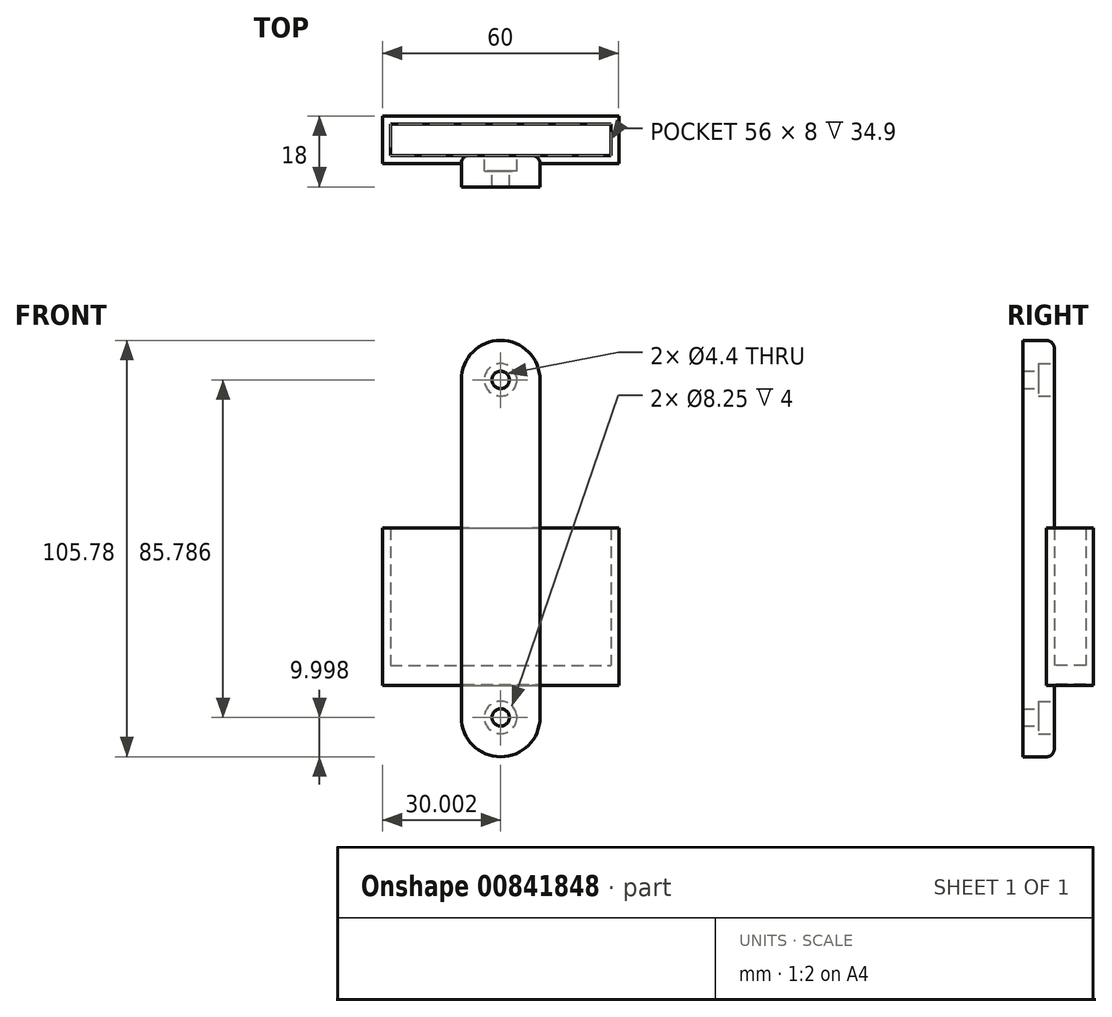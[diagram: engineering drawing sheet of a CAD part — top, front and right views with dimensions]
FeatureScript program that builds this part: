
annotation { "Feature Type Name" : "Feature", "Feature Type Description" : "" }
export const myFeature = defineFeature(function(context is Context, id is Id, definition is map)
    precondition{}
    {
        {
            var Q0;
            Q0=qCreatedBy(makeId("Top.planeOp"),FACE);
            var sketch = newSketch(context, id + "F0", { "sketchPlane" : qUnion([Q0])});
            skLineSegment(sketch, "E0.bottom", {"start": v(-46.7, 10) * mm, "end": v(-26.7, 10) * mm});
            skLineSegment(sketch, "E0.top", {"start": v(-46.7, -2) * mm, "end": v(13.3, -2) * mm});
            skLineSegment(sketch, "E0.left", {"start": v(-46.7, 10) * mm, "end": v(-46.7, -2) * mm});
            skLineSegment(sketch, "E0.right", {"start": v(13.3, 10) * mm, "end": v(13.3, -2) * mm});
            skLineSegment(sketch, "E1.bottom", {"start": v(-44.7, 8) * mm, "end": v(11.3, 8) * mm});
            skLineSegment(sketch, "E1.top", {"start": v(-44.7, 0) * mm, "end": v(11.3, 0) * mm});
            skLineSegment(sketch, "E1.left", {"start": v(-44.7, 8) * mm, "end": v(-44.7, 0) * mm});
            skLineSegment(sketch, "E1.right", {"start": v(11.3, 8) * mm, "end": v(11.3, 0) * mm});
            skPoint(sketch, "E2", {"position": v(-16.7, 10) * mm});
            skLineSegment(sketch, "E3.top", {"start": v(-26.7, 18) * mm, "end": v(-6.7, 18) * mm});
            skLineSegment(sketch, "E3.left", {"start": v(-26.7, 10) * mm, "end": v(-26.7, 18) * mm});
            skLineSegment(sketch, "E3.right", {"start": v(-6.7, 10) * mm, "end": v(-6.7, 18) * mm});
            skLineSegment(sketch, "E4.trimOffspring", {"start": v(-6.7, 10) * mm, "end": v(13.3, 10) * mm});
            skLineSegment(sketch, "E5", {"start": v(-26.7, 10) * mm, "end": v(-6.7, 10) * mm});
            skSolve(sketch);
        }
        {
            var Q0;
            Q0=makeQuery(id+"F0.imprint","IMPRINT",FACE,{"disambiguationData":[TD([[makeQuery(id+"F0.imprint","IMPRINT",EDGE,{"derivedFrom":sQuery(id+"F0.wireOp",EDGE,"E0.bottom")}),-1.0]])]});
            extrude(context, id + "F1", {"entities" : qUnion([Q0]), "endBound" : BoundingType.SYMMETRIC, "depth" : 40 * mm, "offsetDistance" : 25 * mm});
        }
        {
            var Q0;
            Q0=makeQuery(id+"F0.imprint","IMPRINT",FACE,{"disambiguationData":[TD([[makeQuery(id+"F0.imprint","IMPRINT",EDGE,{"derivedFrom":sQuery(id+"F0.wireOp",EDGE,"E1.bottom")}),-1.0]])]});
            extrude(context, id + "F2", {"entities" : qUnion([Q0]), "operationType" : NewBodyOperationType.ADD, "oppositeDirection" : true, "depth" : 19.7 * mm, "offsetDistance" : 25 * mm, "hasSecondDirection" : true, "secondDirectionOppositeDirection" : true, "secondDirectionDepth" : 14.9 * mm});
        }
        {
            var Q0;
            Q0=qCreatedBy(makeId("Front.planeOp"),FACE);
            var sketch = newSketch(context, id + "F3", { "sketchPlane" : qUnion([Q0])});
            skArc(sketch, "E6", {"start": v(-26.7, -28.1) * mm, "mid": v(-16.7, -38.1) * mm, "end": v(-6.7, -28.1) * mm});
            skArc(sketch, "E7", {"start": v(-6.7, 57.68) * mm, "mid": v(-16.7, 67.68) * mm, "end": v(-26.7, 57.68) * mm});
            skLineSegment(sketch, "E8", {"start": v(-6.7, 57.68) * mm, "end": v(-6.7, -28.1) * mm});
            skLineSegment(sketch, "E9", {"start": v(-26.7, 57.68) * mm, "end": v(-26.7, -28.1) * mm});
            skSolve(sketch);
        }
        {
            var Q0;
            Q0 = qSketchRegion(id + "F3", true);
            extrude(context, id + "F4", {"entities" : qUnion([Q0]), "operationType" : NewBodyOperationType.ADD, "depth" : 8 * mm, "offsetDistance" : 25 * mm});
        }
        {
            var Q0;
            Q0=makeQuery(id+"F4.opExtrude","CAP_EDGE",EDGE,{"disambiguationData":[OSD([sQuery(id+"F3.wireOp",EDGE,"E7")])],"isStart":true});
            var Q1;
            {var subQ0=sQuery(id+"F3.wireOp",EDGE,"E8");Q1=makeQuery(id+"F4.boolean.opBoolean","SPLIT",EDGE,{"disambiguationData":[topologyDisambiguationEdgeConnected([makeQuery(id+"F1.opExtrude","SWEPT_FACE",FACE,{"disambiguationData":[OSD([sQuery(id+"F0.wireOp",EDGE,"E1.top")])]}),makeQuery(id+"F4.opExtrude","CAP_FACE",FACE,{"disambiguationData":[OSD([sQuery(id+"F3.wireOp",EDGE,"E6"),sQuery(id+"F3.wireOp",EDGE,"E7"),subQ0,sQuery(id+"F3.wireOp",EDGE,"E9")])],"isStart":true}),makeQuery(id+"F4.opExtrude","SWEPT_FACE",FACE,{"disambiguationData":[OSD([subQ0])]})])],"derivedFrom":makeQuery(id+"F4.opExtrude","CAP_EDGE",EDGE,{"disambiguationData":[OSD([subQ0])],"isStart":true})});}
            var Q2;
            {var subQ0=sQuery(id+"F3.wireOp",EDGE,"E9");Q2=makeQuery(id+"F4.boolean.opBoolean","SPLIT",EDGE,{"disambiguationData":[topologyDisambiguationEdgeConnected([makeQuery(id+"F1.opExtrude","SWEPT_FACE",FACE,{"disambiguationData":[OSD([sQuery(id+"F0.wireOp",EDGE,"E1.top")])]}),makeQuery(id+"F4.opExtrude","CAP_FACE",FACE,{"disambiguationData":[OSD([sQuery(id+"F3.wireOp",EDGE,"E6"),sQuery(id+"F3.wireOp",EDGE,"E7"),sQuery(id+"F3.wireOp",EDGE,"E8"),subQ0])],"isStart":true}),makeQuery(id+"F4.opExtrude","SWEPT_FACE",FACE,{"disambiguationData":[OSD([subQ0])]})])],"derivedFrom":makeQuery(id+"F4.opExtrude","CAP_EDGE",EDGE,{"disambiguationData":[OSD([subQ0])],"isStart":true})});}
            fillet(context, id + "F5", {"entities" : qUnion([Q0, Q1, Q2]), "radius" : 2 * mm, "allowEdgeOverflow" : false});
        }
        {
            var Q0;
            Q0=makeQuery(id+"F4.opExtrude","CAP_EDGE",EDGE,{"disambiguationData":[OSD([sQuery(id+"F3.wireOp",EDGE,"E6")])],"isStart":true});
            fillet(context, id + "F6", {"entities" : qUnion([Q0]), "radius" : 2 * mm, "tangentPropagation" : true, "allowEdgeOverflow" : false});
        }
        {
            var Q0;
            Q0=sQuery(id+"F3.wireOp",VERTEX,"E7.center");
            var Q1;
            Q1=sQuery(id+"F3.wireOp",VERTEX,"E6.center");
            var Q2;
            Q2=makeQuery(id+"F1.opExtrude","SWEPT_BODY",BODY,{"disambiguationData":[OSD([sQuery(id+"F0.wireOp",EDGE,"E0.bottom"),sQuery(id+"F0.wireOp",EDGE,"E0.top"),sQuery(id+"F0.wireOp",EDGE,"E0.left"),sQuery(id+"F0.wireOp",EDGE,"E0.right"),sQuery(id+"F0.wireOp",EDGE,"E1.bottom"),sQuery(id+"F0.wireOp",EDGE,"E1.top"),sQuery(id+"F0.wireOp",EDGE,"E1.left"),sQuery(id+"F0.wireOp",EDGE,"E1.right"),sQuery(id+"F0.wireOp",EDGE,"E4.trimOffspring"),sQuery(id+"F0.wireOp",EDGE,"E5")])]});
            hole(context, id + "F7", {"style" : HoleStyle.C_BORE, "endStyle" : HoleEndStyle.THROUGH, "oppositeDirection" : true, "standardTappedOrClearance" : lookupTablePath({ "fit" : "Normal", "standard" : "ISO", "size" : "M4", "type" : "Clearance" }), "standardBlindInLast" : lookupTablePath({ "fit" : "Standard", "standard" : "ISO", "size" : "M4", "type" : "Clearance" }), "holeDiameter" : 4.4 * mm, "cBoreDiameter" : 8.25 * mm, "cBoreDepth" : 4 * mm, "majorDiameter" : 3 * mm, "isTappedThrough" : true, "tappedDepth" : 12 * mm, "tapClearance" : 3, "startFromSketch" : true, "locations" : qUnion([Q0, Q1]), "scope" : qUnion([Q2])});
        }
    });
